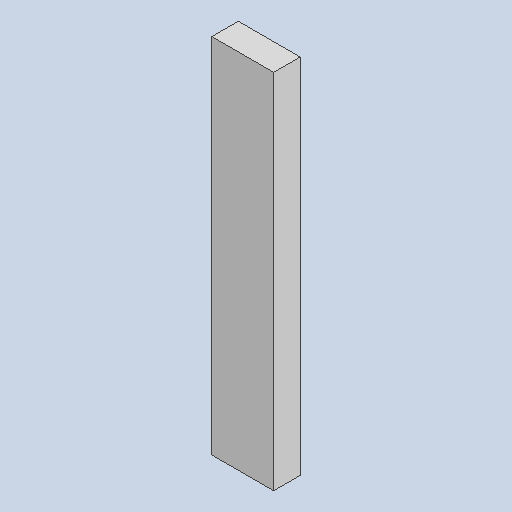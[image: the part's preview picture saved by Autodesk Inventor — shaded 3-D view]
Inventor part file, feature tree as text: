
AUTODESK INVENTOR PART (.ipt)
format: ipt  version: 2025 (Build 290162000, 162)  size: 78,848 bytes
history: native  units: in
note: dims shown in document units (in); Inventor stores cm internally (conversion verified against a paired STEP export)
features: other x3, sketch x1
ambient origin geometry x8: Origin, YZ Plane, XZ Plane, XY Plane, X Axis, Y Axis, Z Axis, Center Point
bodies: Solid1 (feature_tree)
feature tree (4):
  other  "side-side2_MIR.ipt"
  other  "Solid1::side-side2_MIR.ipt"
  other  "TaggingFeature1"
  sketch  "Sketch1"  dims[d0=0.3937in]
